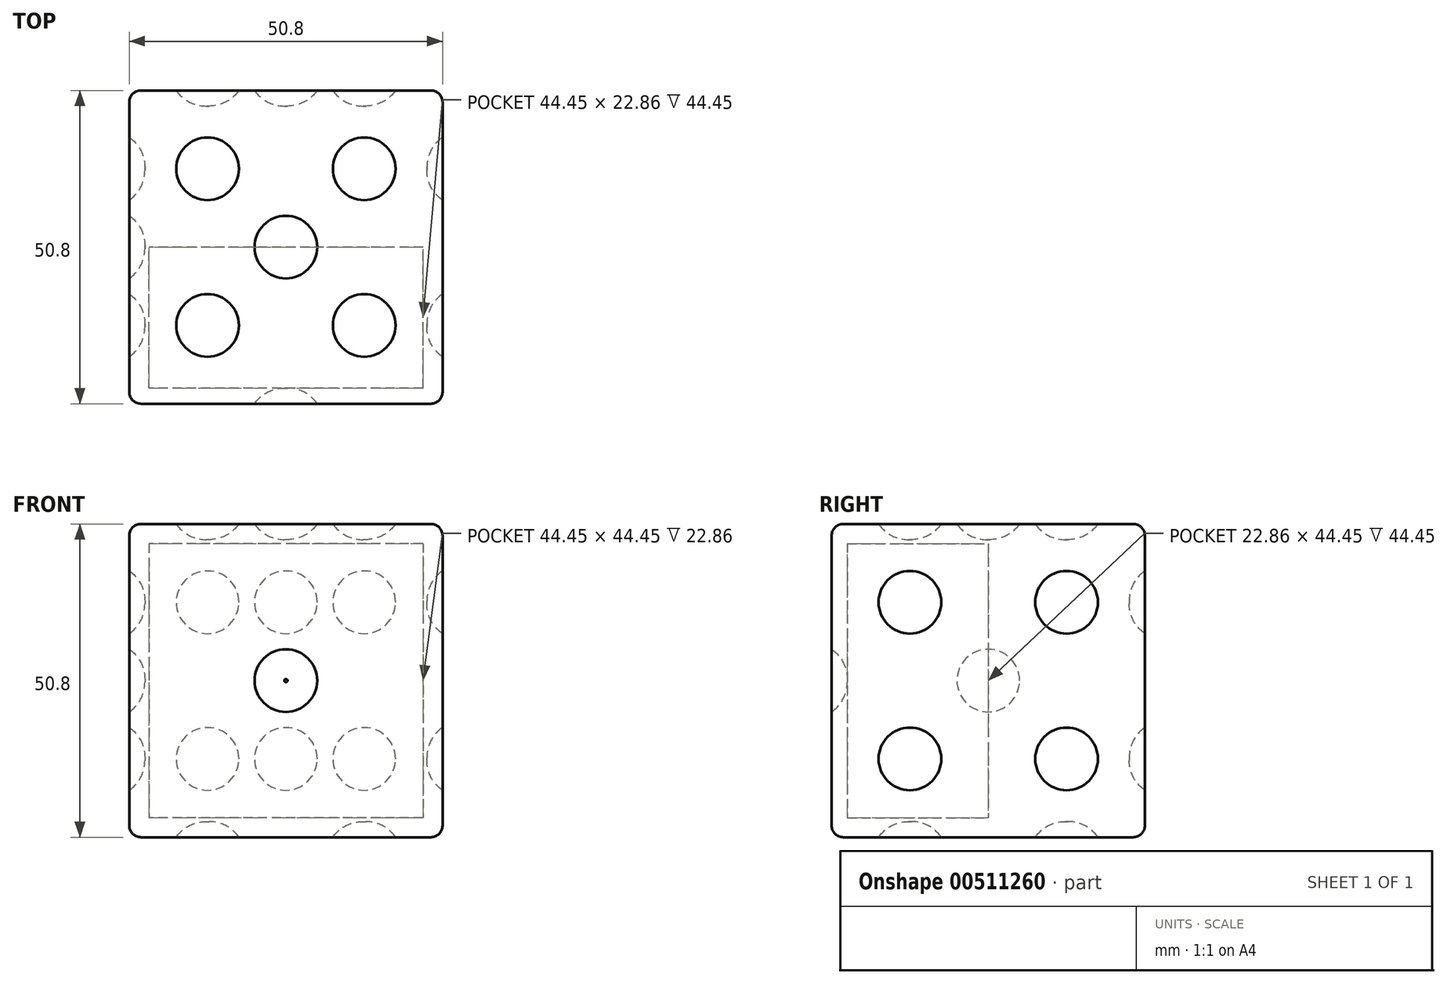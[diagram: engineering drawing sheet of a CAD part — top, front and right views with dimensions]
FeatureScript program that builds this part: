
annotation { "Feature Type Name" : "Feature", "Feature Type Description" : "" }
export const myFeature = defineFeature(function(context is Context, id is Id, definition is map)
    precondition{}
    {
        {
            var Q0;
            Q0=qCreatedBy(makeId("Top.planeOp"),FACE);
            var sketch = newSketch(context, id + "F0", { "sketchPlane" : qUnion([Q0])});
            skLineSegment(sketch, "E0.bottom", {"start": v(0, 0) * mm, "end": v(50.8, 0) * mm});
            skLineSegment(sketch, "E0.top", {"start": v(0, 50.8) * mm, "end": v(50.8, 50.8) * mm});
            skLineSegment(sketch, "E0.left", {"start": v(0, 0) * mm, "end": v(0, 50.8) * mm});
            skLineSegment(sketch, "E0.right", {"start": v(50.8, 0) * mm, "end": v(50.8, 50.8) * mm});
            skSolve(sketch);
        }
        {
            var Q0;
            Q0=makeQuery(id+"F0.imprint","IMPRINT",FACE,{"disambiguationData":[TD([[makeQuery(id+"F0.imprint","IMPRINT",EDGE,{"derivedFrom":sQuery(id+"F0.wireOp",EDGE,"E0.bottom")}),1.0]])]});
            extrude(context, id + "F1", {"entities" : qUnion([Q0]), "depth" : 50.8 * mm});
        }
        {
            var Q0;
            Q0=makeQuery(id+"F1.opExtrude","CAP_FACE",FACE,{"disambiguationData":[OSD([sQuery(id+"F0.wireOp",EDGE,"E0.bottom"),sQuery(id+"F0.wireOp",EDGE,"E0.top"),sQuery(id+"F0.wireOp",EDGE,"E0.left"),sQuery(id+"F0.wireOp",EDGE,"E0.right")])],"isStart":false});
            var sketch = newSketch(context, id + "F2", { "sketchPlane" : qUnion([Q0])});
            skCircle(sketch, "E1", {"center": v(25.4, 25.4) * mm, "radius": 5.08 * mm});
            skCircle(sketch, "E2", {"center": v(12.7, 38.1) * mm, "radius": 5.08 * mm});
            skCircle(sketch, "E3", {"center": v(38.1, 38.1) * mm, "radius": 5.08 * mm});
            skCircle(sketch, "E4", {"center": v(38.1, 12.7) * mm, "radius": 5.08 * mm});
            skCircle(sketch, "E5", {"center": v(12.7, 12.7) * mm, "radius": 5.08 * mm});
            skSolve(sketch);
        }
        {
            var Q0;
            Q0=makeQuery(id+"F2.imprint","IMPRINT",FACE,{"disambiguationData":[TD([[makeQuery(id+"F2.imprint","IMPRINT",EDGE,{"derivedFrom":sQuery(id+"F2.wireOp",EDGE,"E2")}),1.0]])]});
            var Q1;
            Q1=makeQuery(id+"F2.imprint","IMPRINT",FACE,{"disambiguationData":[TD([[makeQuery(id+"F2.imprint","IMPRINT",EDGE,{"derivedFrom":sQuery(id+"F2.wireOp",EDGE,"E3")}),1.0]])]});
            var Q2;
            Q2=makeQuery(id+"F2.imprint","IMPRINT",FACE,{"disambiguationData":[TD([[makeQuery(id+"F2.imprint","IMPRINT",EDGE,{"derivedFrom":sQuery(id+"F2.wireOp",EDGE,"E1")}),1.0]])]});
            var Q3;
            Q3=makeQuery(id+"F2.imprint","IMPRINT",FACE,{"disambiguationData":[TD([[makeQuery(id+"F2.imprint","IMPRINT",EDGE,{"derivedFrom":sQuery(id+"F2.wireOp",EDGE,"E5")}),1.0]])]});
            var Q4;
            Q4=makeQuery(id+"F2.imprint","IMPRINT",FACE,{"disambiguationData":[TD([[makeQuery(id+"F2.imprint","IMPRINT",EDGE,{"derivedFrom":sQuery(id+"F2.wireOp",EDGE,"E4")}),1.0]])]});
            extrude(context, id + "F3", {"entities" : qUnion([Q0, Q1, Q2, Q3, Q4]), "operationType" : NewBodyOperationType.REMOVE, "oppositeDirection" : true, "depth" : 2.54 * mm, "offsetDistance" : 25.4 * mm});
        }
        {
            var Q0;
            Q0=makeQuery(id+"F1.opExtrude","SWEPT_EDGE",EDGE,{"disambiguationData":[OSD([sQuery(id+"F0.wireOp",EDGE,"E0.bottom"),sQuery(id+"F0.wireOp",EDGE,"E0.right")])]});
            var Q1;
            Q1=makeQuery(id+"F1.opExtrude","SWEPT_EDGE",EDGE,{"disambiguationData":[OSD([sQuery(id+"F0.wireOp",EDGE,"E0.top"),sQuery(id+"F0.wireOp",EDGE,"E0.right")])]});
            var Q2;
            Q2=makeQuery(id+"F1.opExtrude","SWEPT_EDGE",EDGE,{"disambiguationData":[OSD([sQuery(id+"F0.wireOp",EDGE,"E0.top"),sQuery(id+"F0.wireOp",EDGE,"E0.left")])]});
            var Q3;
            Q3=makeQuery(id+"F1.opExtrude","SWEPT_EDGE",EDGE,{"disambiguationData":[OSD([sQuery(id+"F0.wireOp",EDGE,"E0.bottom"),sQuery(id+"F0.wireOp",EDGE,"E0.left")])]});
            var Q4;
            Q4=makeQuery(id+"F1.opExtrude","CAP_EDGE",EDGE,{"disambiguationData":[OSD([sQuery(id+"F0.wireOp",EDGE,"E0.top")])],"isStart":false});
            var Q5;
            Q5=makeQuery(id+"F1.opExtrude","CAP_EDGE",EDGE,{"disambiguationData":[OSD([sQuery(id+"F0.wireOp",EDGE,"E0.left")])],"isStart":false});
            var Q6;
            Q6=makeQuery(id+"F1.opExtrude","CAP_EDGE",EDGE,{"disambiguationData":[OSD([sQuery(id+"F0.wireOp",EDGE,"E0.bottom")])],"isStart":false});
            var Q7;
            Q7=makeQuery(id+"F1.opExtrude","CAP_EDGE",EDGE,{"disambiguationData":[OSD([sQuery(id+"F0.wireOp",EDGE,"E0.right")])],"isStart":false});
            var Q8;
            Q8=makeQuery(id+"F1.opExtrude","CAP_EDGE",EDGE,{"disambiguationData":[OSD([sQuery(id+"F0.wireOp",EDGE,"E0.bottom")])],"isStart":true});
            var Q9;
            Q9=makeQuery(id+"F1.opExtrude","CAP_EDGE",EDGE,{"disambiguationData":[OSD([sQuery(id+"F0.wireOp",EDGE,"E0.top")])],"isStart":true});
            var Q10;
            Q10=makeQuery(id+"F1.opExtrude","CAP_EDGE",EDGE,{"disambiguationData":[OSD([sQuery(id+"F0.wireOp",EDGE,"E0.right")])],"isStart":true});
            var Q11;
            Q11=makeQuery(id+"F1.opExtrude","CAP_EDGE",EDGE,{"disambiguationData":[OSD([sQuery(id+"F0.wireOp",EDGE,"E0.left")])],"isStart":true});
            fillet(context, id + "F4", {"entities" : qUnion([Q0, Q1, Q2, Q3, Q4, Q5, Q6, Q7, Q8, Q9, Q10, Q11]), "radius" : 1.9 * mm, "tangentPropagation" : true, "allowEdgeOverflow" : false});
        }
        {
            var Q0;
            Q0=makeQuery(id+"F3.boolean.opBoolean","COPY",EDGE,{"derivedFrom":makeQuery(id+"F3.opExtrude","CAP_EDGE",EDGE,{"disambiguationData":[OSD([sQuery(id+"F2.wireOp",EDGE,"E1")])],"isStart":false})});
            var Q1;
            Q1=makeQuery(id+"F3.boolean.opBoolean","COPY",EDGE,{"derivedFrom":makeQuery(id+"F3.opExtrude","CAP_EDGE",EDGE,{"disambiguationData":[OSD([sQuery(id+"F2.wireOp",EDGE,"E5")])],"isStart":false})});
            var Q2;
            Q2=makeQuery(id+"F3.boolean.opBoolean","COPY",EDGE,{"derivedFrom":makeQuery(id+"F3.opExtrude","CAP_EDGE",EDGE,{"disambiguationData":[OSD([sQuery(id+"F2.wireOp",EDGE,"E4")])],"isStart":false})});
            var Q3;
            Q3=makeQuery(id+"F3.boolean.opBoolean","COPY",EDGE,{"derivedFrom":makeQuery(id+"F3.opExtrude","CAP_EDGE",EDGE,{"disambiguationData":[OSD([sQuery(id+"F2.wireOp",EDGE,"E2")])],"isStart":false})});
            var Q4;
            Q4=makeQuery(id+"F3.boolean.opBoolean","COPY",EDGE,{"derivedFrom":makeQuery(id+"F3.opExtrude","CAP_EDGE",EDGE,{"disambiguationData":[OSD([sQuery(id+"F2.wireOp",EDGE,"E3")])],"isStart":false})});
            fillet(context, id + "F5", {"entities" : qUnion([Q0, Q1, Q2, Q3, Q4]), "radius" : 5.84 * mm, "tangentPropagation" : true, "allowEdgeOverflow" : false});
        }
        {
            var Q0;
            Q0=makeQuery(id+"F1.opExtrude","SWEPT_FACE",FACE,{"disambiguationData":[OSD([sQuery(id+"F0.wireOp",EDGE,"E0.right")])]});
            var sketch = newSketch(context, id + "F6", { "sketchPlane" : qUnion([Q0])});
            skCircle(sketch, "E6", {"center": v(12.7, 12.7) * mm, "radius": 5.08 * mm});
            skCircle(sketch, "E7", {"center": v(12.7, 38.1) * mm, "radius": 5.08 * mm});
            skCircle(sketch, "E8", {"center": v(38.1, 12.7) * mm, "radius": 5.08 * mm});
            skCircle(sketch, "E9", {"center": v(38.1, 38.1) * mm, "radius": 5.08 * mm});
            skSolve(sketch);
        }
        {
            var Q0;
            Q0=makeQuery(id+"F1.opExtrude","CAP_FACE",FACE,{"disambiguationData":[OSD([sQuery(id+"F0.wireOp",EDGE,"E0.bottom"),sQuery(id+"F0.wireOp",EDGE,"E0.top"),sQuery(id+"F0.wireOp",EDGE,"E0.left"),sQuery(id+"F0.wireOp",EDGE,"E0.right")])],"isStart":true});
            var sketch = newSketch(context, id + "F7", { "sketchPlane" : qUnion([Q0])});
            skCircle(sketch, "E10", {"center": v(12.7, -12.7) * mm, "radius": 5.08 * mm});
            skCircle(sketch, "E11", {"center": v(38.1, -38.1) * mm, "radius": 5.08 * mm});
            skLineSegment(sketch, "E12", {"start": v(12.7, -12.7) * mm, "end": v(38.1, -38.1) * mm, "construction": true});
            skSolve(sketch);
        }
        {
            var Q0;
            Q0=makeQuery(id+"F1.opExtrude","SWEPT_FACE",FACE,{"disambiguationData":[OSD([sQuery(id+"F0.wireOp",EDGE,"E0.left")])]});
            var sketch = newSketch(context, id + "F8", { "sketchPlane" : qUnion([Q0])});
            skCircle(sketch, "E13", {"center": v(-12.7, 12.7) * mm, "radius": 5.08 * mm});
            skCircle(sketch, "E14", {"center": v(-38.1, 38.1) * mm, "radius": 5.08 * mm});
            skLineSegment(sketch, "E15", {"start": v(-38.1, 38.1) * mm, "end": v(-12.7, 12.7) * mm, "construction": true});
            skCircle(sketch, "E16", {"center": v(-25.4, 25.4) * mm, "radius": 5.08 * mm});
            skSolve(sketch);
        }
        {
            var Q0;
            Q0=makeQuery(id+"F1.opExtrude","SWEPT_FACE",FACE,{"disambiguationData":[OSD([sQuery(id+"F0.wireOp",EDGE,"E0.top")])]});
            var sketch = newSketch(context, id + "F9", { "sketchPlane" : qUnion([Q0])});
            skCircle(sketch, "E17", {"center": v(-38.1, 12.7) * mm, "radius": 5.08 * mm});
            skCircle(sketch, "E18", {"center": v(-12.7, 12.7) * mm, "radius": 5.08 * mm});
            skCircle(sketch, "E19", {"center": v(-38.1, 38.1) * mm, "radius": 5.08 * mm});
            skCircle(sketch, "E20", {"center": v(-12.7, 38.1) * mm, "radius": 5.08 * mm});
            skLineSegment(sketch, "E21", {"start": v(-38.1, 12.7) * mm, "end": v(-12.7, 12.7) * mm, "construction": true});
            skCircle(sketch, "E22", {"center": v(-25.4, 12.7) * mm, "radius": 5.08 * mm});
            skLineSegment(sketch, "E23", {"start": v(-38.1, 38.1) * mm, "end": v(-12.7, 38.1) * mm, "construction": true});
            skCircle(sketch, "E24", {"center": v(-25.4, 38.1) * mm, "radius": 5.08 * mm});
            skSolve(sketch);
        }
        {
            var Q0;
            Q0=makeQuery(id+"F1.opExtrude","SWEPT_FACE",FACE,{"disambiguationData":[OSD([sQuery(id+"F0.wireOp",EDGE,"E0.bottom")])]});
            var sketch = newSketch(context, id + "F10", { "sketchPlane" : qUnion([Q0])});
            skLineSegment(sketch, "E25", {"start": v(25.4, 48.9) * mm, "end": v(25.4, 1.9) * mm, "construction": true});
            skLineSegment(sketch, "E26", {"start": v(48.9, 25.4) * mm, "end": v(1.9, 25.4) * mm, "construction": true});
            skCircle(sketch, "E27", {"center": v(25.4, 25.4) * mm, "radius": 5.08 * mm});
            skSolve(sketch);
        }
        {
            var Q0;
            Q0 = qSketchRegion(id + "F10", true);
            extrude(context, id + "F11", {"entities" : qUnion([Q0]), "operationType" : NewBodyOperationType.REMOVE, "oppositeDirection" : true, "depth" : 2.54 * mm, "offsetDistance" : 25.4 * mm});
        }
        {
            var Q0;
            Q0 = qSketchRegion(id + "F9", true);
            extrude(context, id + "F12", {"entities" : qUnion([Q0]), "operationType" : NewBodyOperationType.REMOVE, "oppositeDirection" : true, "depth" : 2.54 * mm, "offsetDistance" : 25.4 * mm});
        }
        {
            var Q0;
            Q0 = qSketchRegion(id + "F8", true);
            extrude(context, id + "F13", {"entities" : qUnion([Q0]), "operationType" : NewBodyOperationType.REMOVE, "oppositeDirection" : true, "depth" : 2.54 * mm, "offsetDistance" : 25.4 * mm});
        }
        {
            var Q0;
            Q0 = qSketchRegion(id + "F7", true);
            extrude(context, id + "F14", {"entities" : qUnion([Q0]), "operationType" : NewBodyOperationType.REMOVE, "oppositeDirection" : true, "depth" : 2.54 * mm, "offsetDistance" : 25.4 * mm});
        }
        {
            var Q0;
            Q0 = qSketchRegion(id + "F6", true);
            extrude(context, id + "F15", {"entities" : qUnion([Q0]), "operationType" : NewBodyOperationType.REMOVE, "oppositeDirection" : true, "depth" : 2.54 * mm, "offsetDistance" : 25.4 * mm});
        }
        {
            var Q0;
            Q0=makeQuery(id+"F15.boolean.opBoolean","COPY",FACE,{"derivedFrom":makeQuery(id+"F15.opExtrude","CAP_FACE",FACE,{"disambiguationData":[OSD([sQuery(id+"F6.wireOp",EDGE,"E7")])],"isStart":false})});
            var Q1;
            Q1=makeQuery(id+"F15.boolean.opBoolean","COPY",EDGE,{"derivedFrom":makeQuery(id+"F15.opExtrude","CAP_EDGE",EDGE,{"disambiguationData":[OSD([sQuery(id+"F6.wireOp",EDGE,"E9")])],"isStart":false})});
            var Q2;
            Q2=makeQuery(id+"F15.boolean.opBoolean","COPY",FACE,{"derivedFrom":makeQuery(id+"F15.opExtrude","CAP_FACE",FACE,{"disambiguationData":[OSD([sQuery(id+"F6.wireOp",EDGE,"E6")])],"isStart":false})});
            var Q3;
            Q3=makeQuery(id+"F15.boolean.opBoolean","COPY",EDGE,{"derivedFrom":makeQuery(id+"F15.opExtrude","CAP_EDGE",EDGE,{"disambiguationData":[OSD([sQuery(id+"F6.wireOp",EDGE,"E8")])],"isStart":false})});
            var Q4;
            Q4=makeQuery(id+"F12.boolean.opBoolean","COPY",FACE,{"derivedFrom":makeQuery(id+"F12.opExtrude","CAP_FACE",FACE,{"disambiguationData":[OSD([sQuery(id+"F9.wireOp",EDGE,"E19")])],"isStart":false})});
            var Q5;
            Q5=makeQuery(id+"F12.boolean.opBoolean","COPY",EDGE,{"derivedFrom":makeQuery(id+"F12.opExtrude","CAP_EDGE",EDGE,{"disambiguationData":[OSD([sQuery(id+"F9.wireOp",EDGE,"E24")])],"isStart":false})});
            var Q6;
            Q6=makeQuery(id+"F12.boolean.opBoolean","COPY",FACE,{"derivedFrom":makeQuery(id+"F12.opExtrude","CAP_FACE",FACE,{"disambiguationData":[OSD([sQuery(id+"F9.wireOp",EDGE,"E20")])],"isStart":false})});
            var Q7;
            Q7=makeQuery(id+"F12.boolean.opBoolean","COPY",FACE,{"derivedFrom":makeQuery(id+"F12.opExtrude","CAP_FACE",FACE,{"disambiguationData":[OSD([sQuery(id+"F9.wireOp",EDGE,"E17")])],"isStart":false})});
            var Q8;
            Q8=makeQuery(id+"F12.boolean.opBoolean","COPY",FACE,{"derivedFrom":makeQuery(id+"F12.opExtrude","CAP_FACE",FACE,{"disambiguationData":[OSD([sQuery(id+"F9.wireOp",EDGE,"E22")])],"isStart":false})});
            var Q9;
            Q9=makeQuery(id+"F12.boolean.opBoolean","COPY",FACE,{"derivedFrom":makeQuery(id+"F12.opExtrude","CAP_FACE",FACE,{"disambiguationData":[OSD([sQuery(id+"F9.wireOp",EDGE,"E18")])],"isStart":false})});
            var Q10;
            Q10=makeQuery(id+"F13.boolean.opBoolean","COPY",FACE,{"derivedFrom":makeQuery(id+"F13.opExtrude","CAP_FACE",FACE,{"disambiguationData":[OSD([sQuery(id+"F8.wireOp",EDGE,"E14")])],"isStart":false})});
            var Q11;
            Q11=makeQuery(id+"F13.boolean.opBoolean","COPY",FACE,{"derivedFrom":makeQuery(id+"F13.opExtrude","CAP_FACE",FACE,{"disambiguationData":[OSD([sQuery(id+"F8.wireOp",EDGE,"E16")])],"isStart":false})});
            var Q12;
            Q12=makeQuery(id+"F13.boolean.opBoolean","COPY",FACE,{"derivedFrom":makeQuery(id+"F13.opExtrude","CAP_FACE",FACE,{"disambiguationData":[OSD([sQuery(id+"F8.wireOp",EDGE,"E13")])],"isStart":false})});
            var Q13;
            Q13=makeQuery(id+"F11.boolean.opBoolean","COPY",FACE,{"derivedFrom":makeQuery(id+"F11.opExtrude","CAP_FACE",FACE,{"disambiguationData":[OSD([sQuery(id+"F10.wireOp",EDGE,"E27")])],"isStart":false})});
            var Q14;
            Q14=makeQuery(id+"F14.boolean.opBoolean","COPY",FACE,{"derivedFrom":makeQuery(id+"F14.opExtrude","CAP_FACE",FACE,{"disambiguationData":[OSD([sQuery(id+"F7.wireOp",EDGE,"E10")])],"isStart":false})});
            var Q15;
            Q15=makeQuery(id+"F14.boolean.opBoolean","COPY",FACE,{"derivedFrom":makeQuery(id+"F14.opExtrude","CAP_FACE",FACE,{"disambiguationData":[OSD([sQuery(id+"F7.wireOp",EDGE,"Qo6tsoL7-wil2-XItr-77vd-AbzDAJDmsIUF")])],"isStart":false})});
            var Q16;
            Q16=makeQuery(id+"F14.boolean.opBoolean","COPY",FACE,{"derivedFrom":makeQuery(id+"F14.opExtrude","CAP_FACE",FACE,{"disambiguationData":[OSD([sQuery(id+"F7.wireOp",EDGE,"E11")])],"isStart":false})});
            fillet(context, id + "F16", {"entities" : qUnion([Q0, Q1, Q2, Q3, Q4, Q5, Q6, Q7, Q8, Q9, Q10, Q11, Q12, Q13, Q14, Q15, Q16]), "radius" : 5.84 * mm, "tangentPropagation" : true, "allowEdgeOverflow" : false});
        }
        {
            var Q0;
            Q0=qCreatedBy(makeId("Front.planeOp"),FACE);
            cPlane(context, id + "F17", {"entities" : qUnion([Q0]), "cplaneType" : CPlaneType.OFFSET, "offset" : 25.4 * mm, "oppositeDirection" : true, "width" : 152.4 * mm, "height" : 152.4 * mm});
        }
        {
            var Q0;
            Q0=qCreatedBy(id+"F17.planeOp",FACE);
            var sketch = newSketch(context, id + "F18", { "sketchPlane" : qUnion([Q0])});
            skLineSegment(sketch, "E28.bottom", {"start": v(47.62, 47.62) * mm, "end": v(3.17, 47.62) * mm});
            skLineSegment(sketch, "E28.top", {"start": v(47.62, 3.18) * mm, "end": v(3.18, 3.18) * mm});
            skLineSegment(sketch, "E28.left", {"start": v(47.62, 47.63) * mm, "end": v(47.62, 3.18) * mm});
            skLineSegment(sketch, "E28.right", {"start": v(3.17, 47.63) * mm, "end": v(3.18, 3.18) * mm});
            skSolve(sketch);
        }
        {
            var Q0;
            Q0 = qSketchRegion(id + "F18", true);
            extrude(context, id + "F19", {"entities" : qUnion([Q0]), "operationType" : NewBodyOperationType.REMOVE, "depth" : 22.86 * mm, "offsetDistance" : 25.4 * mm});
        }
    });
